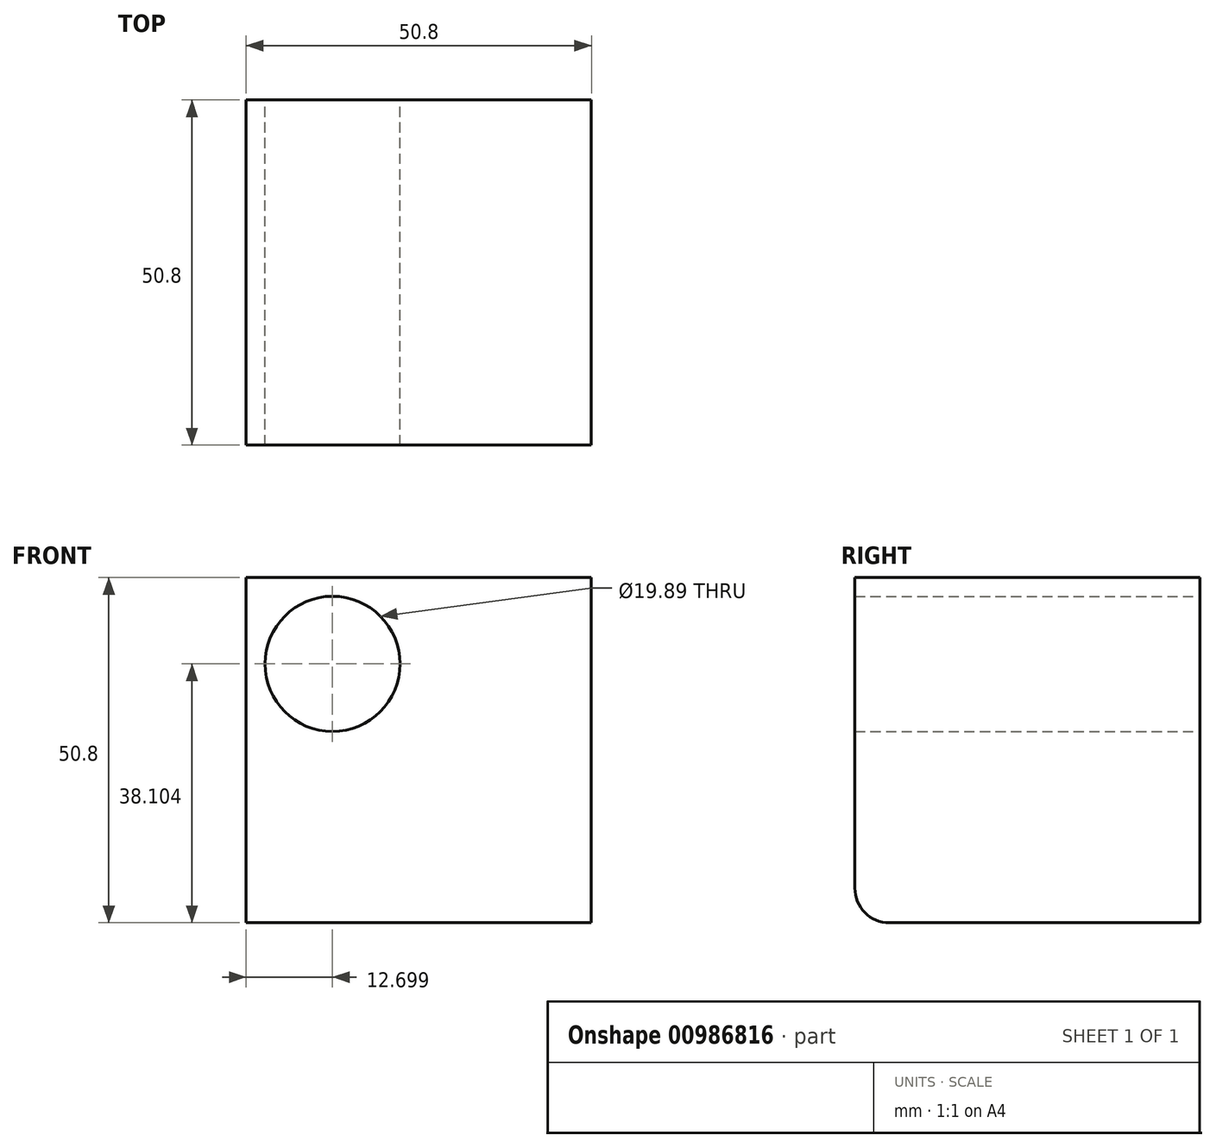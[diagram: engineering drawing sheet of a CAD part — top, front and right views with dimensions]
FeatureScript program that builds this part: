
annotation { "Feature Type Name" : "Feature", "Feature Type Description" : "" }
export const myFeature = defineFeature(function(context is Context, id is Id, definition is map)
    precondition{}
    {
        {
            var Q0;
            Q0=qCreatedBy(makeId("Front.planeOp"),FACE);
            var sketch = newSketch(context, id + "F0", { "sketchPlane" : qUnion([Q0])});
            skLineSegment(sketch, "E0.bottom", {"start": v(-34.4, 28.05) * mm, "end": v(16.4, 28.05) * mm});
            skLineSegment(sketch, "E0.top", {"start": v(-34.4, -22.75) * mm, "end": v(16.4, -22.75) * mm});
            skLineSegment(sketch, "E0.left", {"start": v(-34.4, 28.05) * mm, "end": v(-34.4, -22.75) * mm});
            skLineSegment(sketch, "E0.right", {"start": v(16.4, 28.05) * mm, "end": v(16.4, -22.75) * mm});
            skCircle(sketch, "E1", {"center": v(-21.7, 15.35) * mm, "radius": 9.95 * mm});
            skSolve(sketch);
        }
        {
            var Q0;
            Q0=makeQuery(id+"F0.imprint","IMPRINT",FACE,{"disambiguationData":[TD([[makeQuery(id+"F0.imprint","IMPRINT",EDGE,{"derivedFrom":sQuery(id+"F0.wireOp",EDGE,"E0.bottom")}),-1.0]])]});
            extrude(context, id + "F1", {"entities" : qUnion([Q0]), "depth" : 50.8 * mm, "offsetDistance" : 25.4 * mm});
        }
        {
            var Q0;
            Q0=makeQuery(id+"F1.opExtrude","CAP_EDGE",EDGE,{"disambiguationData":[OSD([sQuery(id+"F0.wireOp",EDGE,"E0.top")])],"isStart":false});
            fillet(context, id + "F2", {"entities" : qUnion([Q0]), "radius" : 5.08 * mm, "tangentPropagation" : true, "allowEdgeOverflow" : false});
        }
    });
